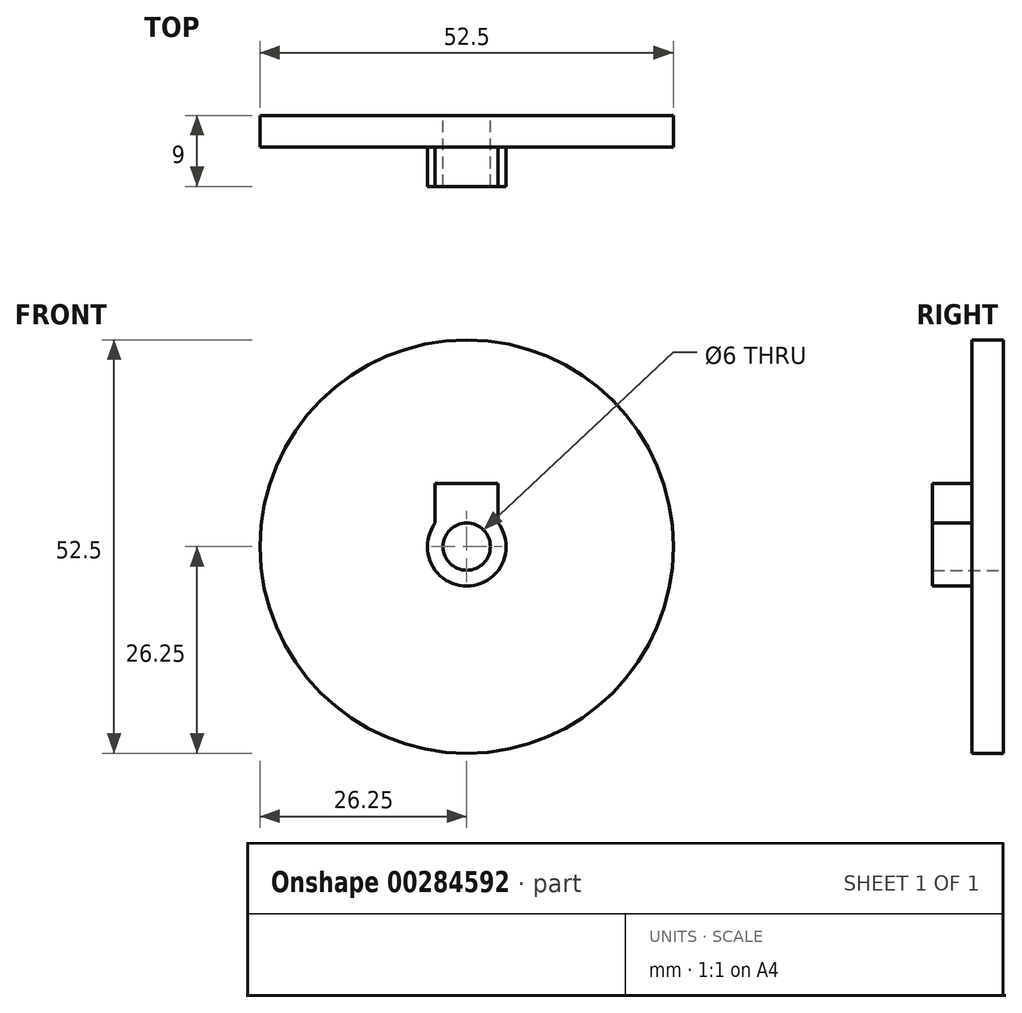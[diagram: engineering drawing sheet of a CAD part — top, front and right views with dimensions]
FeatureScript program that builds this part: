
annotation { "Feature Type Name" : "Feature", "Feature Type Description" : "" }
export const myFeature = defineFeature(function(context is Context, id is Id, definition is map)
    precondition{}
    {
        {
            var Q0;
            Q0=qCreatedBy(makeId("Front.planeOp"),FACE);
            var sketch = newSketch(context, id + "F0", { "sketchPlane" : qUnion([Q0])});
            skCircle(sketch, "E0", {"center": v(0, 0) * mm, "radius": 26.25 * mm});
            skCircle(sketch, "E1", {"center": v(0, 0) * mm, "radius": 3 * mm});
            skSolve(sketch);
        }
        {
            var Q0;
            Q0=qSketchRegion(id+"F0",true);
            extrude(context, id + "F1", {"entities" : qUnion([Q0]), "depth" : 4 * mm});
        }
        {
            var Q0;
            Q0=makeQuery(id+"F1.opExtrude","CAP_FACE",FACE,{"disambiguationData":[OSD([sQuery(id+"F0.wireOp",EDGE,"E0"),sQuery(id+"F0.wireOp",EDGE,"E1")])],"isStart":false});
            var sketch = newSketch(context, id + "F2", { "sketchPlane" : qUnion([Q0])});
            skCircle(sketch, "E2", {"center": v(0, 0) * mm, "radius": 3 * mm});
            skArc(sketch, "E3", {"start": v(-4, 3) * mm, "mid": v(0, -5) * mm, "end": v(4, 3) * mm});
            skLineSegment(sketch, "E4", {"start": v(-4, 3) * mm, "end": v(-4, 8) * mm});
            skLineSegment(sketch, "E5", {"start": v(-4, 8) * mm, "end": v(4, 8) * mm});
            skLineSegment(sketch, "E6", {"start": v(4, 8) * mm, "end": v(4, 3) * mm});
            skLineSegment(sketch, "E7", {"start": v(-4, 3) * mm, "end": v(4, 3) * mm, "construction": true});
            skSolve(sketch);
        }
        {
            var Q0;
            Q0=qSketchRegion(id+"F2",true);
            extrude(context, id + "F3", {"entities" : qUnion([Q0]), "operationType" : NewBodyOperationType.ADD, "depth" : 5 * mm});
        }
    });
